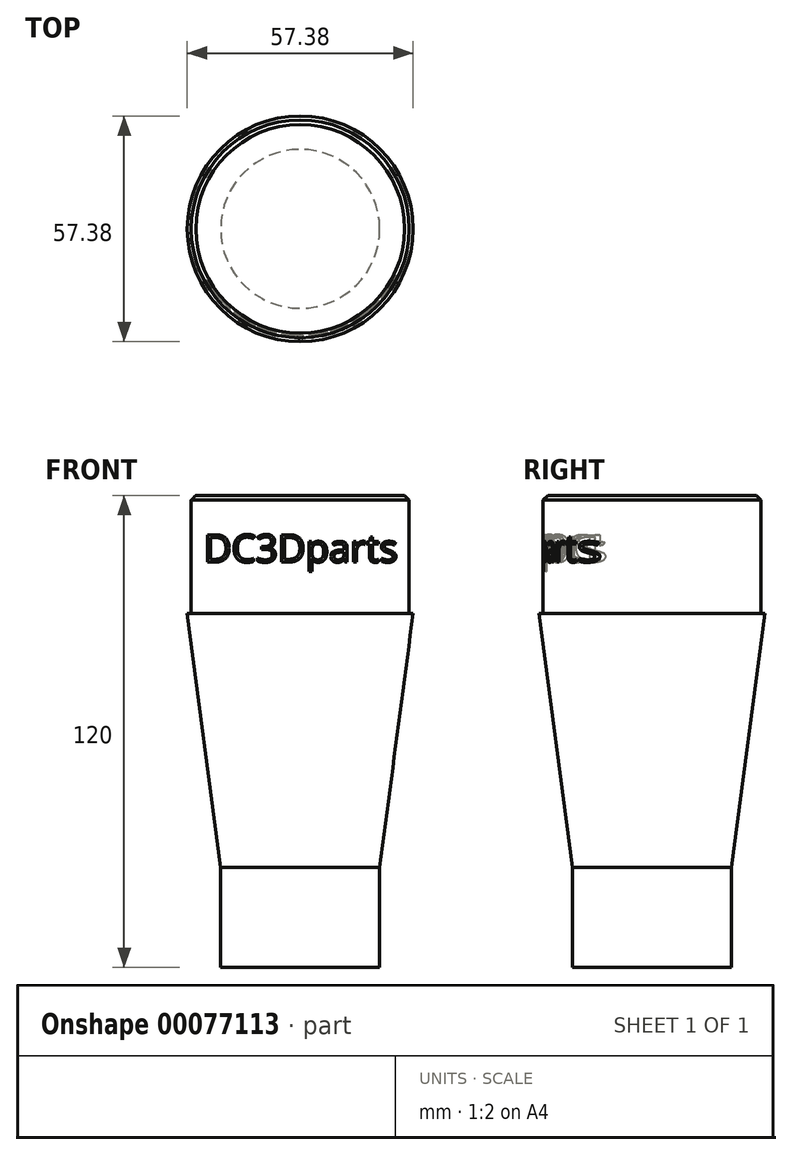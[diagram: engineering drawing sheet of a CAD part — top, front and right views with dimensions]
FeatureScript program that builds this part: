
annotation { "Feature Type Name" : "Feature", "Feature Type Description" : "" }
export const myFeature = defineFeature(function(context is Context, id is Id, definition is map)
    precondition{}
    {
        {
            var Q0;
            Q0=qCreatedBy(makeId("Front.planeOp"),FACE);
            var sketch = newSketch(context, id + "F0", { "sketchPlane" : qUnion([Q0])});
            skLineSegment(sketch, "E0", {"start": v(-27.68, 73.27) * mm, "end": v(-27.68, 43.27) * mm});
            skLineSegment(sketch, "E1", {"start": v(-27.68, 43.27) * mm, "end": v(-28.68, 43.27) * mm});
            skLineSegment(sketch, "E2", {"start": v(-28.68, 43.27) * mm, "end": v(-20.2, -21.3) * mm});
            skLineSegment(sketch, "E3", {"start": v(-20.2, -21.3) * mm, "end": v(-20.2, -46.73) * mm});
            skLineSegment(sketch, "E4", {"start": v(-20.2, -46.73) * mm, "end": v(0, -46.73) * mm});
            skLineSegment(sketch, "E5", {"start": v(-27.68, 73.27) * mm, "end": v(0, 73.27) * mm});
            skLineSegment(sketch, "E6", {"start": v(0, 94.78) * mm, "end": v(0, -99.97) * mm, "construction": true});
            skLineSegment(sketch, "E7", {"start": v(0, 73.27) * mm, "end": v(0, -46.73) * mm});
            skPoint(sketch, "E8.start.orphan", {"position": v(-20.8, -16.73) * mm});
            skPoint(sketch, "E9.orphan", {"position": v(-20.2, -16.73) * mm});
            skSolve(sketch);
        }
        {
            var Q0;
            Q0=makeQuery(id+"F0.imprint","IMPRINT",FACE,{"disambiguationData":[TD([[makeQuery(id+"F0.imprint","IMPRINT",EDGE,{"derivedFrom":sQuery(id+"F0.wireOp",EDGE,"E0")}),1.0]])]});
            var Q1;
            Q1=sQuery(id+"F0.wireOp",EDGE,"E6");
            revolve(context, id + "F1", {"entities" : qUnion([Q0]), "axis" : qUnion([Q1]), "revolveType" : RevolveType.FULL});
        }
        {
            var Q0;
            Q0=makeQuery(id+"F1.opRevolve","SWEPT_EDGE",EDGE,{"disambiguationData":[OSD([sQuery(id+"F0.wireOp",EDGE,"E0"),sQuery(id+"F0.wireOp",EDGE,"E5")])]});
            chamfer(context, id + "F2", {"entities" : qUnion([Q0]), "width" : 1.2 * mm, "tangentPropagation" : true});
        }
        {
            var Q0;
            Q0=qCreatedBy(makeId("Front.planeOp"),FACE);
            cPlane(context, id + "F3", {"entities" : qUnion([Q0]), "cplaneType" : CPlaneType.OFFSET, "offset" : 40 * mm, "width" : 150 * mm, "height" : 150 * mm});
        }
        {
            var Q0;
            Q0=qCreatedBy(id+"F3.planeOp",FACE);
            var sketch = newSketch(context, id + "F4", { "sketchPlane" : qUnion([Q0])});
            skText(sketch, "E10", { "text": "DC3Dparts", "fontName": "OpenSans-Regular.ttf"});
            const initialGuessF4  = {"E10": [-0.02451, 0.0563, 1, 0, 0.007]};
            skSetInitialGuess(sketch, initialGuessF4);
            skSolve(sketch);
        }
        {
            var Q0;
            Q0 = qSketchRegion(id + "F4", true);
            var Q1;
            Q1=qCreatedBy(makeId("Front.planeOp"),FACE);
            extrude(context, id + "F5", {"entities" : qUnion([Q0]), "endBound" : BoundingType.UP_TO_SURFACE, "oppositeDirection" : true, "depth" : 25 * mm, "endBoundEntityFace" : qUnion([Q1]), "offsetDistance" : 25 * mm});
        }
        {
            var Q0;
            Q0=qCreatedBy(makeId("Front.planeOp"),FACE);
            var sketch = newSketch(context, id + "F6", { "sketchPlane" : qUnion([Q0])});
            skLineSegment(sketch, "E11.bottom", {"start": v(0, 49.2) * mm, "end": v(-27, 49.2) * mm});
            skLineSegment(sketch, "E11.top", {"start": v(0, 81.79) * mm, "end": v(-27, 81.79) * mm});
            skLineSegment(sketch, "E11.left", {"start": v(0, 49.2) * mm, "end": v(0, 81.79) * mm});
            skLineSegment(sketch, "E11.right", {"start": v(-27, 49.2) * mm, "end": v(-27, 81.79) * mm});
            skSolve(sketch);
        }
        {
            var Q0;
            Q0=makeQuery(id+"F6.imprint","IMPRINT",FACE,{"disambiguationData":[TD([[makeQuery(id+"F6.imprint","IMPRINT",EDGE,{"derivedFrom":sQuery(id+"F6.wireOp",EDGE,"E11.bottom")}),-1.0]])]});
            var Q1;
            Q1=sQuery(id+"F6.wireOp",EDGE,"E11.left");
            revolve(context, id + "F7", {"entities" : qUnion([Q0]), "axis" : qUnion([Q1]), "revolveType" : RevolveType.FULL});
        }
        {
            var Q0;
            Q0=makeQuery(id+"F7.opRevolve","SWEPT_BODY",BODY,{"disambiguationData":[OSD([sQuery(id+"F6.wireOp",EDGE,"E11.bottom"),sQuery(id+"F6.wireOp",EDGE,"E11.top"),sQuery(id+"F6.wireOp",EDGE,"E11.left"),sQuery(id+"F6.wireOp",EDGE,"E11.right")])]});
            var Q1;
            Q1=makeQuery(id+"F5.opExtrude","SWEPT_BODY",BODY,{"disambiguationData":[OSD([sQuery(id+"F4.wireOp",EDGE,"E10.sketch_text.stroke-0"),sQuery(id+"F4.wireOp",EDGE,"E10.sketch_text.stroke-1"),sQuery(id+"F4.wireOp",EDGE,"E10.sketch_text.stroke-2"),sQuery(id+"F4.wireOp",EDGE,"E10.sketch_text.stroke-3"),sQuery(id+"F4.wireOp",EDGE,"E10.sketch_text.stroke-4"),sQuery(id+"F4.wireOp",EDGE,"E10.sketch_text.stroke-5"),sQuery(id+"F4.wireOp",EDGE,"E10.sketch_text.stroke-6"),sQuery(id+"F4.wireOp",EDGE,"E10.sketch_text.stroke-7"),sQuery(id+"F4.wireOp",EDGE,"E10.sketch_text.stroke-8"),sQuery(id+"F4.wireOp",EDGE,"E10.sketch_text.stroke-9"),sQuery(id+"F4.wireOp",EDGE,"E10.sketch_text.stroke-10"),sQuery(id+"F4.wireOp",EDGE,"E10.sketch_text.stroke-11"),sQuery(id+"F4.wireOp",EDGE,"E10.sketch_text.stroke-12"),sQuery(id+"F4.wireOp",EDGE,"E10.sketch_text.stroke-13")])]});
            var Q2;
            Q2=makeQuery(id+"F5.opExtrude","SWEPT_BODY",BODY,{"disambiguationData":[OSD([sQuery(id+"F4.wireOp",EDGE,"E10.sketch_text.stroke-14"),sQuery(id+"F4.wireOp",EDGE,"E10.sketch_text.stroke-15"),sQuery(id+"F4.wireOp",EDGE,"E10.sketch_text.stroke-16"),sQuery(id+"F4.wireOp",EDGE,"E10.sketch_text.stroke-17"),sQuery(id+"F4.wireOp",EDGE,"E10.sketch_text.stroke-18"),sQuery(id+"F4.wireOp",EDGE,"E10.sketch_text.stroke-19"),sQuery(id+"F4.wireOp",EDGE,"E10.sketch_text.stroke-20"),sQuery(id+"F4.wireOp",EDGE,"E10.sketch_text.stroke-21"),sQuery(id+"F4.wireOp",EDGE,"E10.sketch_text.stroke-22"),sQuery(id+"F4.wireOp",EDGE,"E10.sketch_text.stroke-23"),sQuery(id+"F4.wireOp",EDGE,"E10.sketch_text.stroke-24"),sQuery(id+"F4.wireOp",EDGE,"E10.sketch_text.stroke-25"),sQuery(id+"F4.wireOp",EDGE,"E10.sketch_text.stroke-26"),sQuery(id+"F4.wireOp",EDGE,"E10.sketch_text.stroke-27"),sQuery(id+"F4.wireOp",EDGE,"E10.sketch_text.stroke-28")])]});
            var Q3;
            Q3=makeQuery(id+"F5.opExtrude","SWEPT_BODY",BODY,{"disambiguationData":[OSD([sQuery(id+"F4.wireOp",EDGE,"E10.sketch_text.stroke-29"),sQuery(id+"F4.wireOp",EDGE,"E10.sketch_text.stroke-30"),sQuery(id+"F4.wireOp",EDGE,"E10.sketch_text.stroke-31"),sQuery(id+"F4.wireOp",EDGE,"E10.sketch_text.stroke-32"),sQuery(id+"F4.wireOp",EDGE,"E10.sketch_text.stroke-33"),sQuery(id+"F4.wireOp",EDGE,"E10.sketch_text.stroke-34"),sQuery(id+"F4.wireOp",EDGE,"E10.sketch_text.stroke-35"),sQuery(id+"F4.wireOp",EDGE,"E10.sketch_text.stroke-36"),sQuery(id+"F4.wireOp",EDGE,"E10.sketch_text.stroke-37"),sQuery(id+"F4.wireOp",EDGE,"E10.sketch_text.stroke-38"),sQuery(id+"F4.wireOp",EDGE,"E10.sketch_text.stroke-39"),sQuery(id+"F4.wireOp",EDGE,"E10.sketch_text.stroke-40"),sQuery(id+"F4.wireOp",EDGE,"E10.sketch_text.stroke-41"),sQuery(id+"F4.wireOp",EDGE,"E10.sketch_text.stroke-42"),sQuery(id+"F4.wireOp",EDGE,"E10.sketch_text.stroke-43"),sQuery(id+"F4.wireOp",EDGE,"E10.sketch_text.stroke-44"),sQuery(id+"F4.wireOp",EDGE,"E10.sketch_text.stroke-45"),sQuery(id+"F4.wireOp",EDGE,"E10.sketch_text.stroke-46"),sQuery(id+"F4.wireOp",EDGE,"E10.sketch_text.stroke-47"),sQuery(id+"F4.wireOp",EDGE,"E10.sketch_text.stroke-48"),sQuery(id+"F4.wireOp",EDGE,"E10.sketch_text.stroke-49"),sQuery(id+"F4.wireOp",EDGE,"E10.sketch_text.stroke-50"),sQuery(id+"F4.wireOp",EDGE,"E10.sketch_text.stroke-51"),sQuery(id+"F4.wireOp",EDGE,"E10.sketch_text.stroke-52"),sQuery(id+"F4.wireOp",EDGE,"E10.sketch_text.stroke-53"),sQuery(id+"F4.wireOp",EDGE,"E10.sketch_text.stroke-54"),sQuery(id+"F4.wireOp",EDGE,"E10.sketch_text.stroke-55"),sQuery(id+"F4.wireOp",EDGE,"E10.sketch_text.stroke-56")])]});
            var Q4;
            Q4=makeQuery(id+"F5.opExtrude","SWEPT_BODY",BODY,{"disambiguationData":[OSD([sQuery(id+"F4.wireOp",EDGE,"E10.sketch_text.stroke-57"),sQuery(id+"F4.wireOp",EDGE,"E10.sketch_text.stroke-58"),sQuery(id+"F4.wireOp",EDGE,"E10.sketch_text.stroke-59"),sQuery(id+"F4.wireOp",EDGE,"E10.sketch_text.stroke-60"),sQuery(id+"F4.wireOp",EDGE,"E10.sketch_text.stroke-61"),sQuery(id+"F4.wireOp",EDGE,"E10.sketch_text.stroke-62"),sQuery(id+"F4.wireOp",EDGE,"E10.sketch_text.stroke-63"),sQuery(id+"F4.wireOp",EDGE,"E10.sketch_text.stroke-64"),sQuery(id+"F4.wireOp",EDGE,"E10.sketch_text.stroke-65"),sQuery(id+"F4.wireOp",EDGE,"E10.sketch_text.stroke-66"),sQuery(id+"F4.wireOp",EDGE,"E10.sketch_text.stroke-67"),sQuery(id+"F4.wireOp",EDGE,"E10.sketch_text.stroke-68"),sQuery(id+"F4.wireOp",EDGE,"E10.sketch_text.stroke-69"),sQuery(id+"F4.wireOp",EDGE,"E10.sketch_text.stroke-70")])]});
            var Q5;
            Q5=makeQuery(id+"F5.opExtrude","SWEPT_BODY",BODY,{"disambiguationData":[OSD([sQuery(id+"F4.wireOp",EDGE,"E10.sketch_text.stroke-71"),sQuery(id+"F4.wireOp",EDGE,"E10.sketch_text.stroke-72"),sQuery(id+"F4.wireOp",EDGE,"E10.sketch_text.stroke-73"),sQuery(id+"F4.wireOp",EDGE,"E10.sketch_text.stroke-74"),sQuery(id+"F4.wireOp",EDGE,"E10.sketch_text.stroke-75"),sQuery(id+"F4.wireOp",EDGE,"E10.sketch_text.stroke-76"),sQuery(id+"F4.wireOp",EDGE,"E10.sketch_text.stroke-77"),sQuery(id+"F4.wireOp",EDGE,"E10.sketch_text.stroke-78"),sQuery(id+"F4.wireOp",EDGE,"E10.sketch_text.stroke-79"),sQuery(id+"F4.wireOp",EDGE,"E10.sketch_text.stroke-80"),sQuery(id+"F4.wireOp",EDGE,"E10.sketch_text.stroke-81"),sQuery(id+"F4.wireOp",EDGE,"E10.sketch_text.stroke-82"),sQuery(id+"F4.wireOp",EDGE,"E10.sketch_text.stroke-83"),sQuery(id+"F4.wireOp",EDGE,"E10.sketch_text.stroke-84"),sQuery(id+"F4.wireOp",EDGE,"E10.sketch_text.stroke-85"),sQuery(id+"F4.wireOp",EDGE,"E10.sketch_text.stroke-86"),sQuery(id+"F4.wireOp",EDGE,"E10.sketch_text.stroke-87"),sQuery(id+"F4.wireOp",EDGE,"E10.sketch_text.stroke-88"),sQuery(id+"F4.wireOp",EDGE,"E10.sketch_text.stroke-89"),sQuery(id+"F4.wireOp",EDGE,"E10.sketch_text.stroke-90"),sQuery(id+"F4.wireOp",EDGE,"E10.sketch_text.stroke-91"),sQuery(id+"F4.wireOp",EDGE,"E10.sketch_text.stroke-92"),sQuery(id+"F4.wireOp",EDGE,"E10.sketch_text.stroke-93"),sQuery(id+"F4.wireOp",EDGE,"E10.sketch_text.stroke-94"),sQuery(id+"F4.wireOp",EDGE,"E10.sketch_text.stroke-95")])]});
            var Q6;
            Q6=makeQuery(id+"F5.opExtrude","SWEPT_BODY",BODY,{"disambiguationData":[OSD([sQuery(id+"F4.wireOp",EDGE,"E10.sketch_text.stroke-96"),sQuery(id+"F4.wireOp",EDGE,"E10.sketch_text.stroke-97"),sQuery(id+"F4.wireOp",EDGE,"E10.sketch_text.stroke-98"),sQuery(id+"F4.wireOp",EDGE,"E10.sketch_text.stroke-99"),sQuery(id+"F4.wireOp",EDGE,"E10.sketch_text.stroke-100"),sQuery(id+"F4.wireOp",EDGE,"E10.sketch_text.stroke-101"),sQuery(id+"F4.wireOp",EDGE,"E10.sketch_text.stroke-102"),sQuery(id+"F4.wireOp",EDGE,"E10.sketch_text.stroke-103"),sQuery(id+"F4.wireOp",EDGE,"E10.sketch_text.stroke-104"),sQuery(id+"F4.wireOp",EDGE,"E10.sketch_text.stroke-105"),sQuery(id+"F4.wireOp",EDGE,"E10.sketch_text.stroke-106"),sQuery(id+"F4.wireOp",EDGE,"E10.sketch_text.stroke-107"),sQuery(id+"F4.wireOp",EDGE,"E10.sketch_text.stroke-108"),sQuery(id+"F4.wireOp",EDGE,"E10.sketch_text.stroke-109"),sQuery(id+"F4.wireOp",EDGE,"E10.sketch_text.stroke-110"),sQuery(id+"F4.wireOp",EDGE,"E10.sketch_text.stroke-111"),sQuery(id+"F4.wireOp",EDGE,"E10.sketch_text.stroke-112"),sQuery(id+"F4.wireOp",EDGE,"E10.sketch_text.stroke-113"),sQuery(id+"F4.wireOp",EDGE,"E10.sketch_text.stroke-114"),sQuery(id+"F4.wireOp",EDGE,"E10.sketch_text.stroke-115"),sQuery(id+"F4.wireOp",EDGE,"E10.sketch_text.stroke-116"),sQuery(id+"F4.wireOp",EDGE,"E10.sketch_text.stroke-117"),sQuery(id+"F4.wireOp",EDGE,"E10.sketch_text.stroke-118"),sQuery(id+"F4.wireOp",EDGE,"E10.sketch_text.stroke-119"),sQuery(id+"F4.wireOp",EDGE,"E10.sketch_text.stroke-120"),sQuery(id+"F4.wireOp",EDGE,"E10.sketch_text.stroke-121"),sQuery(id+"F4.wireOp",EDGE,"E10.sketch_text.stroke-122")])]});
            var Q7;
            Q7=makeQuery(id+"F5.opExtrude","SWEPT_BODY",BODY,{"disambiguationData":[OSD([sQuery(id+"F4.wireOp",EDGE,"E10.sketch_text.stroke-123"),sQuery(id+"F4.wireOp",EDGE,"E10.sketch_text.stroke-124"),sQuery(id+"F4.wireOp",EDGE,"E10.sketch_text.stroke-125"),sQuery(id+"F4.wireOp",EDGE,"E10.sketch_text.stroke-126"),sQuery(id+"F4.wireOp",EDGE,"E10.sketch_text.stroke-127"),sQuery(id+"F4.wireOp",EDGE,"E10.sketch_text.stroke-128"),sQuery(id+"F4.wireOp",EDGE,"E10.sketch_text.stroke-129"),sQuery(id+"F4.wireOp",EDGE,"E10.sketch_text.stroke-130"),sQuery(id+"F4.wireOp",EDGE,"E10.sketch_text.stroke-131"),sQuery(id+"F4.wireOp",EDGE,"E10.sketch_text.stroke-132"),sQuery(id+"F4.wireOp",EDGE,"E10.sketch_text.stroke-133"),sQuery(id+"F4.wireOp",EDGE,"E10.sketch_text.stroke-134"),sQuery(id+"F4.wireOp",EDGE,"E10.sketch_text.stroke-135")])]});
            var Q8;
            Q8=makeQuery(id+"F5.opExtrude","SWEPT_BODY",BODY,{"disambiguationData":[OSD([sQuery(id+"F4.wireOp",EDGE,"E10.sketch_text.stroke-136"),sQuery(id+"F4.wireOp",EDGE,"E10.sketch_text.stroke-137"),sQuery(id+"F4.wireOp",EDGE,"E10.sketch_text.stroke-138"),sQuery(id+"F4.wireOp",EDGE,"E10.sketch_text.stroke-139"),sQuery(id+"F4.wireOp",EDGE,"E10.sketch_text.stroke-140"),sQuery(id+"F4.wireOp",EDGE,"E10.sketch_text.stroke-141"),sQuery(id+"F4.wireOp",EDGE,"E10.sketch_text.stroke-142"),sQuery(id+"F4.wireOp",EDGE,"E10.sketch_text.stroke-143"),sQuery(id+"F4.wireOp",EDGE,"E10.sketch_text.stroke-144"),sQuery(id+"F4.wireOp",EDGE,"E10.sketch_text.stroke-145"),sQuery(id+"F4.wireOp",EDGE,"E10.sketch_text.stroke-146"),sQuery(id+"F4.wireOp",EDGE,"E10.sketch_text.stroke-147"),sQuery(id+"F4.wireOp",EDGE,"E10.sketch_text.stroke-148"),sQuery(id+"F4.wireOp",EDGE,"E10.sketch_text.stroke-149"),sQuery(id+"F4.wireOp",EDGE,"E10.sketch_text.stroke-150"),sQuery(id+"F4.wireOp",EDGE,"E10.sketch_text.stroke-151"),sQuery(id+"F4.wireOp",EDGE,"E10.sketch_text.stroke-152"),sQuery(id+"F4.wireOp",EDGE,"E10.sketch_text.stroke-153"),sQuery(id+"F4.wireOp",EDGE,"E10.sketch_text.stroke-154")])]});
            var Q9;
            Q9=makeQuery(id+"F5.opExtrude","SWEPT_BODY",BODY,{"disambiguationData":[OSD([sQuery(id+"F4.wireOp",EDGE,"E10.sketch_text.stroke-155"),sQuery(id+"F4.wireOp",EDGE,"E10.sketch_text.stroke-156"),sQuery(id+"F4.wireOp",EDGE,"E10.sketch_text.stroke-157"),sQuery(id+"F4.wireOp",EDGE,"E10.sketch_text.stroke-158"),sQuery(id+"F4.wireOp",EDGE,"E10.sketch_text.stroke-159"),sQuery(id+"F4.wireOp",EDGE,"E10.sketch_text.stroke-160"),sQuery(id+"F4.wireOp",EDGE,"E10.sketch_text.stroke-161"),sQuery(id+"F4.wireOp",EDGE,"E10.sketch_text.stroke-162"),sQuery(id+"F4.wireOp",EDGE,"E10.sketch_text.stroke-163"),sQuery(id+"F4.wireOp",EDGE,"E10.sketch_text.stroke-164"),sQuery(id+"F4.wireOp",EDGE,"E10.sketch_text.stroke-165"),sQuery(id+"F4.wireOp",EDGE,"E10.sketch_text.stroke-166"),sQuery(id+"F4.wireOp",EDGE,"E10.sketch_text.stroke-167"),sQuery(id+"F4.wireOp",EDGE,"E10.sketch_text.stroke-168"),sQuery(id+"F4.wireOp",EDGE,"E10.sketch_text.stroke-169"),sQuery(id+"F4.wireOp",EDGE,"E10.sketch_text.stroke-170"),sQuery(id+"F4.wireOp",EDGE,"E10.sketch_text.stroke-171"),sQuery(id+"F4.wireOp",EDGE,"E10.sketch_text.stroke-172"),sQuery(id+"F4.wireOp",EDGE,"E10.sketch_text.stroke-173"),sQuery(id+"F4.wireOp",EDGE,"E10.sketch_text.stroke-174"),sQuery(id+"F4.wireOp",EDGE,"E10.sketch_text.stroke-175"),sQuery(id+"F4.wireOp",EDGE,"E10.sketch_text.stroke-176"),sQuery(id+"F4.wireOp",EDGE,"E10.sketch_text.stroke-177"),sQuery(id+"F4.wireOp",EDGE,"E10.sketch_text.stroke-178"),sQuery(id+"F4.wireOp",EDGE,"E10.sketch_text.stroke-179")])]});
            booleanBodies(context, id + "F8", {"operationType" : BooleanOperationType.SUBTRACTION, "tools" : qUnion([Q0]), "targets" : qUnion([Q1, Q2, Q3, Q4, Q5, Q6, Q7, Q8, Q9])});
        }
        {
            var Q0;
            Q0=makeQuery(id+"F5.opExtrude","SWEPT_BODY",BODY,{"disambiguationData":[OSD([sQuery(id+"F4.wireOp",EDGE,"E10.sketch_text.stroke-0"),sQuery(id+"F4.wireOp",EDGE,"E10.sketch_text.stroke-1"),sQuery(id+"F4.wireOp",EDGE,"E10.sketch_text.stroke-2"),sQuery(id+"F4.wireOp",EDGE,"E10.sketch_text.stroke-3"),sQuery(id+"F4.wireOp",EDGE,"E10.sketch_text.stroke-4"),sQuery(id+"F4.wireOp",EDGE,"E10.sketch_text.stroke-5"),sQuery(id+"F4.wireOp",EDGE,"E10.sketch_text.stroke-6"),sQuery(id+"F4.wireOp",EDGE,"E10.sketch_text.stroke-7"),sQuery(id+"F4.wireOp",EDGE,"E10.sketch_text.stroke-8"),sQuery(id+"F4.wireOp",EDGE,"E10.sketch_text.stroke-9"),sQuery(id+"F4.wireOp",EDGE,"E10.sketch_text.stroke-10"),sQuery(id+"F4.wireOp",EDGE,"E10.sketch_text.stroke-11"),sQuery(id+"F4.wireOp",EDGE,"E10.sketch_text.stroke-12"),sQuery(id+"F4.wireOp",EDGE,"E10.sketch_text.stroke-13")])]});
            var Q1;
            Q1=makeQuery(id+"F5.opExtrude","SWEPT_BODY",BODY,{"disambiguationData":[OSD([sQuery(id+"F4.wireOp",EDGE,"E10.sketch_text.stroke-14"),sQuery(id+"F4.wireOp",EDGE,"E10.sketch_text.stroke-15"),sQuery(id+"F4.wireOp",EDGE,"E10.sketch_text.stroke-16"),sQuery(id+"F4.wireOp",EDGE,"E10.sketch_text.stroke-17"),sQuery(id+"F4.wireOp",EDGE,"E10.sketch_text.stroke-18"),sQuery(id+"F4.wireOp",EDGE,"E10.sketch_text.stroke-19"),sQuery(id+"F4.wireOp",EDGE,"E10.sketch_text.stroke-20"),sQuery(id+"F4.wireOp",EDGE,"E10.sketch_text.stroke-21"),sQuery(id+"F4.wireOp",EDGE,"E10.sketch_text.stroke-22"),sQuery(id+"F4.wireOp",EDGE,"E10.sketch_text.stroke-23"),sQuery(id+"F4.wireOp",EDGE,"E10.sketch_text.stroke-24"),sQuery(id+"F4.wireOp",EDGE,"E10.sketch_text.stroke-25"),sQuery(id+"F4.wireOp",EDGE,"E10.sketch_text.stroke-26"),sQuery(id+"F4.wireOp",EDGE,"E10.sketch_text.stroke-27"),sQuery(id+"F4.wireOp",EDGE,"E10.sketch_text.stroke-28")])]});
            var Q2;
            Q2=makeQuery(id+"F5.opExtrude","SWEPT_BODY",BODY,{"disambiguationData":[OSD([sQuery(id+"F4.wireOp",EDGE,"E10.sketch_text.stroke-29"),sQuery(id+"F4.wireOp",EDGE,"E10.sketch_text.stroke-30"),sQuery(id+"F4.wireOp",EDGE,"E10.sketch_text.stroke-31"),sQuery(id+"F4.wireOp",EDGE,"E10.sketch_text.stroke-32"),sQuery(id+"F4.wireOp",EDGE,"E10.sketch_text.stroke-33"),sQuery(id+"F4.wireOp",EDGE,"E10.sketch_text.stroke-34"),sQuery(id+"F4.wireOp",EDGE,"E10.sketch_text.stroke-35"),sQuery(id+"F4.wireOp",EDGE,"E10.sketch_text.stroke-36"),sQuery(id+"F4.wireOp",EDGE,"E10.sketch_text.stroke-37"),sQuery(id+"F4.wireOp",EDGE,"E10.sketch_text.stroke-38"),sQuery(id+"F4.wireOp",EDGE,"E10.sketch_text.stroke-39"),sQuery(id+"F4.wireOp",EDGE,"E10.sketch_text.stroke-40"),sQuery(id+"F4.wireOp",EDGE,"E10.sketch_text.stroke-41"),sQuery(id+"F4.wireOp",EDGE,"E10.sketch_text.stroke-42"),sQuery(id+"F4.wireOp",EDGE,"E10.sketch_text.stroke-43"),sQuery(id+"F4.wireOp",EDGE,"E10.sketch_text.stroke-44"),sQuery(id+"F4.wireOp",EDGE,"E10.sketch_text.stroke-45"),sQuery(id+"F4.wireOp",EDGE,"E10.sketch_text.stroke-46"),sQuery(id+"F4.wireOp",EDGE,"E10.sketch_text.stroke-47"),sQuery(id+"F4.wireOp",EDGE,"E10.sketch_text.stroke-48"),sQuery(id+"F4.wireOp",EDGE,"E10.sketch_text.stroke-49"),sQuery(id+"F4.wireOp",EDGE,"E10.sketch_text.stroke-50"),sQuery(id+"F4.wireOp",EDGE,"E10.sketch_text.stroke-51"),sQuery(id+"F4.wireOp",EDGE,"E10.sketch_text.stroke-52"),sQuery(id+"F4.wireOp",EDGE,"E10.sketch_text.stroke-53"),sQuery(id+"F4.wireOp",EDGE,"E10.sketch_text.stroke-54"),sQuery(id+"F4.wireOp",EDGE,"E10.sketch_text.stroke-55"),sQuery(id+"F4.wireOp",EDGE,"E10.sketch_text.stroke-56")])]});
            var Q3;
            Q3=makeQuery(id+"F5.opExtrude","SWEPT_BODY",BODY,{"disambiguationData":[OSD([sQuery(id+"F4.wireOp",EDGE,"E10.sketch_text.stroke-57"),sQuery(id+"F4.wireOp",EDGE,"E10.sketch_text.stroke-58"),sQuery(id+"F4.wireOp",EDGE,"E10.sketch_text.stroke-59"),sQuery(id+"F4.wireOp",EDGE,"E10.sketch_text.stroke-60"),sQuery(id+"F4.wireOp",EDGE,"E10.sketch_text.stroke-61"),sQuery(id+"F4.wireOp",EDGE,"E10.sketch_text.stroke-62"),sQuery(id+"F4.wireOp",EDGE,"E10.sketch_text.stroke-63"),sQuery(id+"F4.wireOp",EDGE,"E10.sketch_text.stroke-64"),sQuery(id+"F4.wireOp",EDGE,"E10.sketch_text.stroke-65"),sQuery(id+"F4.wireOp",EDGE,"E10.sketch_text.stroke-66"),sQuery(id+"F4.wireOp",EDGE,"E10.sketch_text.stroke-67"),sQuery(id+"F4.wireOp",EDGE,"E10.sketch_text.stroke-68"),sQuery(id+"F4.wireOp",EDGE,"E10.sketch_text.stroke-69"),sQuery(id+"F4.wireOp",EDGE,"E10.sketch_text.stroke-70")])]});
            var Q4;
            Q4=makeQuery(id+"F5.opExtrude","SWEPT_BODY",BODY,{"disambiguationData":[OSD([sQuery(id+"F4.wireOp",EDGE,"E10.sketch_text.stroke-71"),sQuery(id+"F4.wireOp",EDGE,"E10.sketch_text.stroke-72"),sQuery(id+"F4.wireOp",EDGE,"E10.sketch_text.stroke-73"),sQuery(id+"F4.wireOp",EDGE,"E10.sketch_text.stroke-74"),sQuery(id+"F4.wireOp",EDGE,"E10.sketch_text.stroke-75"),sQuery(id+"F4.wireOp",EDGE,"E10.sketch_text.stroke-76"),sQuery(id+"F4.wireOp",EDGE,"E10.sketch_text.stroke-77"),sQuery(id+"F4.wireOp",EDGE,"E10.sketch_text.stroke-78"),sQuery(id+"F4.wireOp",EDGE,"E10.sketch_text.stroke-79"),sQuery(id+"F4.wireOp",EDGE,"E10.sketch_text.stroke-80"),sQuery(id+"F4.wireOp",EDGE,"E10.sketch_text.stroke-81"),sQuery(id+"F4.wireOp",EDGE,"E10.sketch_text.stroke-82"),sQuery(id+"F4.wireOp",EDGE,"E10.sketch_text.stroke-83"),sQuery(id+"F4.wireOp",EDGE,"E10.sketch_text.stroke-84"),sQuery(id+"F4.wireOp",EDGE,"E10.sketch_text.stroke-85"),sQuery(id+"F4.wireOp",EDGE,"E10.sketch_text.stroke-86"),sQuery(id+"F4.wireOp",EDGE,"E10.sketch_text.stroke-87"),sQuery(id+"F4.wireOp",EDGE,"E10.sketch_text.stroke-88"),sQuery(id+"F4.wireOp",EDGE,"E10.sketch_text.stroke-89"),sQuery(id+"F4.wireOp",EDGE,"E10.sketch_text.stroke-90"),sQuery(id+"F4.wireOp",EDGE,"E10.sketch_text.stroke-91"),sQuery(id+"F4.wireOp",EDGE,"E10.sketch_text.stroke-92"),sQuery(id+"F4.wireOp",EDGE,"E10.sketch_text.stroke-93"),sQuery(id+"F4.wireOp",EDGE,"E10.sketch_text.stroke-94"),sQuery(id+"F4.wireOp",EDGE,"E10.sketch_text.stroke-95")])]});
            var Q5;
            Q5=makeQuery(id+"F5.opExtrude","SWEPT_BODY",BODY,{"disambiguationData":[OSD([sQuery(id+"F4.wireOp",EDGE,"E10.sketch_text.stroke-96"),sQuery(id+"F4.wireOp",EDGE,"E10.sketch_text.stroke-97"),sQuery(id+"F4.wireOp",EDGE,"E10.sketch_text.stroke-98"),sQuery(id+"F4.wireOp",EDGE,"E10.sketch_text.stroke-99"),sQuery(id+"F4.wireOp",EDGE,"E10.sketch_text.stroke-100"),sQuery(id+"F4.wireOp",EDGE,"E10.sketch_text.stroke-101"),sQuery(id+"F4.wireOp",EDGE,"E10.sketch_text.stroke-102"),sQuery(id+"F4.wireOp",EDGE,"E10.sketch_text.stroke-103"),sQuery(id+"F4.wireOp",EDGE,"E10.sketch_text.stroke-104"),sQuery(id+"F4.wireOp",EDGE,"E10.sketch_text.stroke-105"),sQuery(id+"F4.wireOp",EDGE,"E10.sketch_text.stroke-106"),sQuery(id+"F4.wireOp",EDGE,"E10.sketch_text.stroke-107"),sQuery(id+"F4.wireOp",EDGE,"E10.sketch_text.stroke-108"),sQuery(id+"F4.wireOp",EDGE,"E10.sketch_text.stroke-109"),sQuery(id+"F4.wireOp",EDGE,"E10.sketch_text.stroke-110"),sQuery(id+"F4.wireOp",EDGE,"E10.sketch_text.stroke-111"),sQuery(id+"F4.wireOp",EDGE,"E10.sketch_text.stroke-112"),sQuery(id+"F4.wireOp",EDGE,"E10.sketch_text.stroke-113"),sQuery(id+"F4.wireOp",EDGE,"E10.sketch_text.stroke-114"),sQuery(id+"F4.wireOp",EDGE,"E10.sketch_text.stroke-115"),sQuery(id+"F4.wireOp",EDGE,"E10.sketch_text.stroke-116"),sQuery(id+"F4.wireOp",EDGE,"E10.sketch_text.stroke-117"),sQuery(id+"F4.wireOp",EDGE,"E10.sketch_text.stroke-118"),sQuery(id+"F4.wireOp",EDGE,"E10.sketch_text.stroke-119"),sQuery(id+"F4.wireOp",EDGE,"E10.sketch_text.stroke-120"),sQuery(id+"F4.wireOp",EDGE,"E10.sketch_text.stroke-121"),sQuery(id+"F4.wireOp",EDGE,"E10.sketch_text.stroke-122")])]});
            var Q6;
            Q6=makeQuery(id+"F5.opExtrude","SWEPT_BODY",BODY,{"disambiguationData":[OSD([sQuery(id+"F4.wireOp",EDGE,"E10.sketch_text.stroke-123"),sQuery(id+"F4.wireOp",EDGE,"E10.sketch_text.stroke-124"),sQuery(id+"F4.wireOp",EDGE,"E10.sketch_text.stroke-125"),sQuery(id+"F4.wireOp",EDGE,"E10.sketch_text.stroke-126"),sQuery(id+"F4.wireOp",EDGE,"E10.sketch_text.stroke-127"),sQuery(id+"F4.wireOp",EDGE,"E10.sketch_text.stroke-128"),sQuery(id+"F4.wireOp",EDGE,"E10.sketch_text.stroke-129"),sQuery(id+"F4.wireOp",EDGE,"E10.sketch_text.stroke-130"),sQuery(id+"F4.wireOp",EDGE,"E10.sketch_text.stroke-131"),sQuery(id+"F4.wireOp",EDGE,"E10.sketch_text.stroke-132"),sQuery(id+"F4.wireOp",EDGE,"E10.sketch_text.stroke-133"),sQuery(id+"F4.wireOp",EDGE,"E10.sketch_text.stroke-134"),sQuery(id+"F4.wireOp",EDGE,"E10.sketch_text.stroke-135")])]});
            var Q7;
            Q7=makeQuery(id+"F5.opExtrude","SWEPT_BODY",BODY,{"disambiguationData":[OSD([sQuery(id+"F4.wireOp",EDGE,"E10.sketch_text.stroke-136"),sQuery(id+"F4.wireOp",EDGE,"E10.sketch_text.stroke-137"),sQuery(id+"F4.wireOp",EDGE,"E10.sketch_text.stroke-138"),sQuery(id+"F4.wireOp",EDGE,"E10.sketch_text.stroke-139"),sQuery(id+"F4.wireOp",EDGE,"E10.sketch_text.stroke-140"),sQuery(id+"F4.wireOp",EDGE,"E10.sketch_text.stroke-141"),sQuery(id+"F4.wireOp",EDGE,"E10.sketch_text.stroke-142"),sQuery(id+"F4.wireOp",EDGE,"E10.sketch_text.stroke-143"),sQuery(id+"F4.wireOp",EDGE,"E10.sketch_text.stroke-144"),sQuery(id+"F4.wireOp",EDGE,"E10.sketch_text.stroke-145"),sQuery(id+"F4.wireOp",EDGE,"E10.sketch_text.stroke-146"),sQuery(id+"F4.wireOp",EDGE,"E10.sketch_text.stroke-147"),sQuery(id+"F4.wireOp",EDGE,"E10.sketch_text.stroke-148"),sQuery(id+"F4.wireOp",EDGE,"E10.sketch_text.stroke-149"),sQuery(id+"F4.wireOp",EDGE,"E10.sketch_text.stroke-150"),sQuery(id+"F4.wireOp",EDGE,"E10.sketch_text.stroke-151"),sQuery(id+"F4.wireOp",EDGE,"E10.sketch_text.stroke-152"),sQuery(id+"F4.wireOp",EDGE,"E10.sketch_text.stroke-153"),sQuery(id+"F4.wireOp",EDGE,"E10.sketch_text.stroke-154")])]});
            var Q8;
            Q8=makeQuery(id+"F5.opExtrude","SWEPT_BODY",BODY,{"disambiguationData":[OSD([sQuery(id+"F4.wireOp",EDGE,"E10.sketch_text.stroke-155"),sQuery(id+"F4.wireOp",EDGE,"E10.sketch_text.stroke-156"),sQuery(id+"F4.wireOp",EDGE,"E10.sketch_text.stroke-157"),sQuery(id+"F4.wireOp",EDGE,"E10.sketch_text.stroke-158"),sQuery(id+"F4.wireOp",EDGE,"E10.sketch_text.stroke-159"),sQuery(id+"F4.wireOp",EDGE,"E10.sketch_text.stroke-160"),sQuery(id+"F4.wireOp",EDGE,"E10.sketch_text.stroke-161"),sQuery(id+"F4.wireOp",EDGE,"E10.sketch_text.stroke-162"),sQuery(id+"F4.wireOp",EDGE,"E10.sketch_text.stroke-163"),sQuery(id+"F4.wireOp",EDGE,"E10.sketch_text.stroke-164"),sQuery(id+"F4.wireOp",EDGE,"E10.sketch_text.stroke-165"),sQuery(id+"F4.wireOp",EDGE,"E10.sketch_text.stroke-166"),sQuery(id+"F4.wireOp",EDGE,"E10.sketch_text.stroke-167"),sQuery(id+"F4.wireOp",EDGE,"E10.sketch_text.stroke-168"),sQuery(id+"F4.wireOp",EDGE,"E10.sketch_text.stroke-169"),sQuery(id+"F4.wireOp",EDGE,"E10.sketch_text.stroke-170"),sQuery(id+"F4.wireOp",EDGE,"E10.sketch_text.stroke-171"),sQuery(id+"F4.wireOp",EDGE,"E10.sketch_text.stroke-172"),sQuery(id+"F4.wireOp",EDGE,"E10.sketch_text.stroke-173"),sQuery(id+"F4.wireOp",EDGE,"E10.sketch_text.stroke-174"),sQuery(id+"F4.wireOp",EDGE,"E10.sketch_text.stroke-175"),sQuery(id+"F4.wireOp",EDGE,"E10.sketch_text.stroke-176"),sQuery(id+"F4.wireOp",EDGE,"E10.sketch_text.stroke-177"),sQuery(id+"F4.wireOp",EDGE,"E10.sketch_text.stroke-178"),sQuery(id+"F4.wireOp",EDGE,"E10.sketch_text.stroke-179")])]});
            var Q9;
            Q9=makeQuery(id+"F1.opRevolve","SWEPT_BODY",BODY,{"disambiguationData":[OSD([sQuery(id+"F0.wireOp",EDGE,"E0"),sQuery(id+"F0.wireOp",EDGE,"E1"),sQuery(id+"F0.wireOp",EDGE,"E2"),sQuery(id+"F0.wireOp",EDGE,"E3"),sQuery(id+"F0.wireOp",EDGE,"E4"),sQuery(id+"F0.wireOp",EDGE,"E5"),sQuery(id+"F0.wireOp",EDGE,"E7")])]});
            booleanBodies(context, id + "F9", {"operationType" : BooleanOperationType.SUBTRACTION, "tools" : qUnion([Q0, Q1, Q2, Q3, Q4, Q5, Q6, Q7, Q8]), "targets" : qUnion([Q9])});
        }
    });
